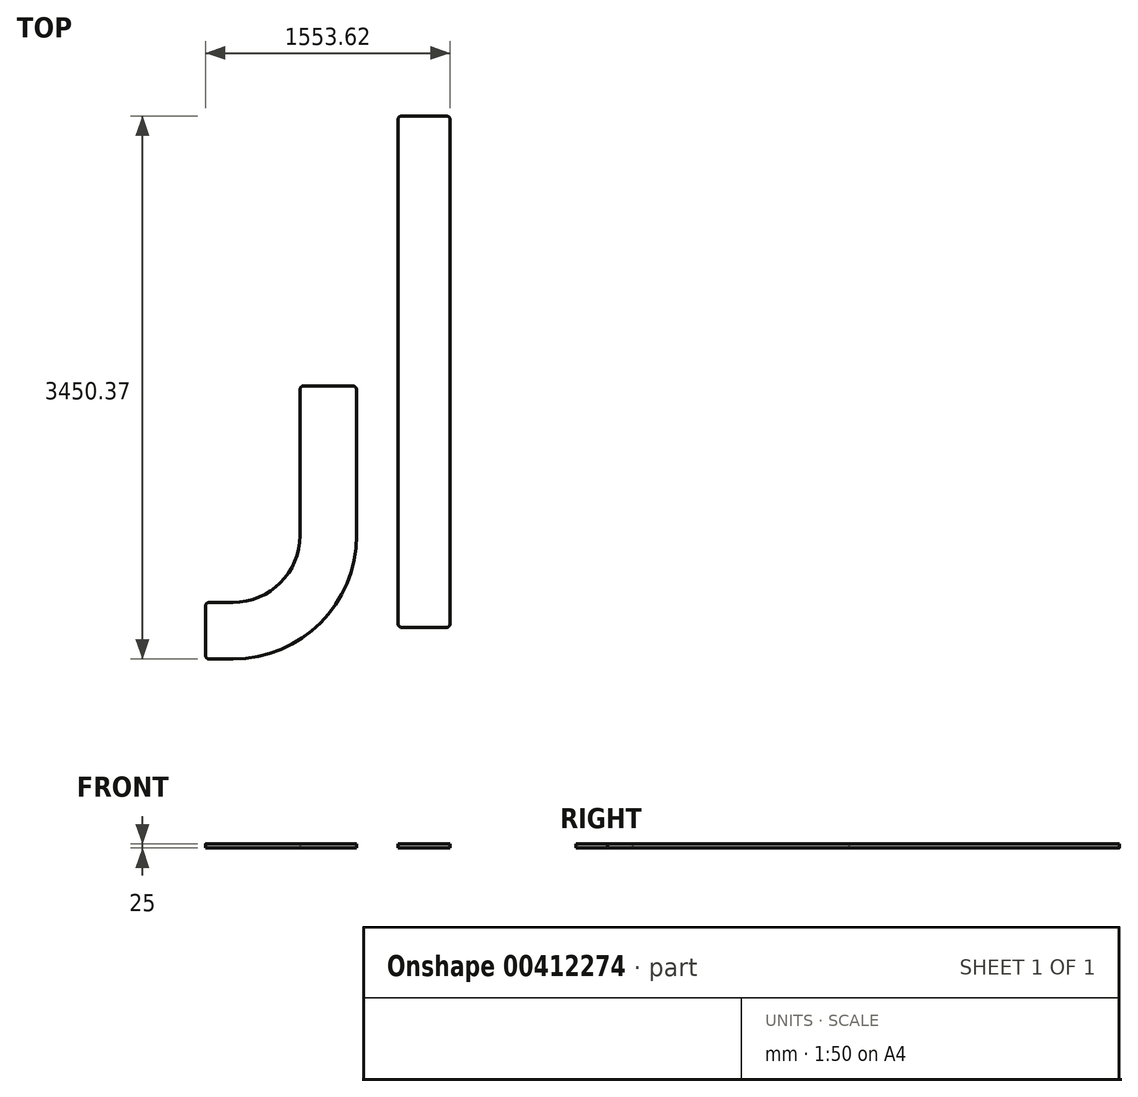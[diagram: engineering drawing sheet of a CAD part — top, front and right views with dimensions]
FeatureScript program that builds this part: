
annotation { "Feature Type Name" : "Feature", "Feature Type Description" : "" }
export const myFeature = defineFeature(function(context is Context, id is Id, definition is map)
    precondition{}
    {
        {
            var Q0;
            Q0=qCreatedBy(makeId("Top.planeOp"),FACE);
            var sketch = newSketch(context, id + "F0", { "sketchPlane" : qUnion([Q0])});
            skLineSegment(sketch, "E0.top", {"start": v(0, 950) * mm, "end": v(360, 950) * mm});
            skLineSegment(sketch, "E0.left", {"start": v(0, 0) * mm, "end": v(0, 950) * mm});
            skLineSegment(sketch, "E0.right", {"start": v(360, 0) * mm, "end": v(360, 950) * mm});
            skArc(sketch, "E1", {"start": v(-425, -425) * mm, "mid": v(-124.48, -300.52) * mm, "end": v(0, 0) * mm});
            skArc(sketch, "E2", {"start": v(-425, -785) * mm, "mid": v(130.08, -555.08) * mm, "end": v(360, 0) * mm});
            skLineSegment(sketch, "E3", {"start": v(-425, -425) * mm, "end": v(-600, -425) * mm});
            skLineSegment(sketch, "E4", {"start": v(-425, -785) * mm, "end": v(-600, -785) * mm});
            skLineSegment(sketch, "E5", {"start": v(-600, -785) * mm, "end": v(-600, -425) * mm});
            skSolve(sketch);
        }
        {
            var Q0;
            Q0=makeQuery(id+"F0.imprint","IMPRINT",FACE,{"disambiguationData":[TD([[makeQuery(id+"F0.imprint","IMPRINT",EDGE,{"derivedFrom":sQuery(id+"F0.wireOp",EDGE,"E0.top")}),-1.0]])]});
            extrude(context, id + "F1", {"entities" : qUnion([Q0]), "depth" : 25 * mm});
        }
        {
            var Q0;
            Q0=makeQuery(id+"F1.opExtrude","SWEPT_EDGE",EDGE,{"disambiguationData":[OSD([sQuery(id+"F0.wireOp",EDGE,"E0.top"),sQuery(id+"F0.wireOp",EDGE,"E0.left")])]});
            var Q1;
            Q1=makeQuery(id+"F1.opExtrude","SWEPT_EDGE",EDGE,{"disambiguationData":[OSD([sQuery(id+"F0.wireOp",EDGE,"E0.top"),sQuery(id+"F0.wireOp",EDGE,"E0.right")])]});
            var Q2;
            Q2=makeQuery(id+"F1.opExtrude","SWEPT_EDGE",EDGE,{"disambiguationData":[OSD([sQuery(id+"F0.wireOp",EDGE,"E4"),sQuery(id+"F0.wireOp",EDGE,"E5")])]});
            var Q3;
            Q3=makeQuery(id+"F1.opExtrude","SWEPT_EDGE",EDGE,{"disambiguationData":[OSD([sQuery(id+"F0.wireOp",EDGE,"E3"),sQuery(id+"F0.wireOp",EDGE,"E5")])]});
            fillet(context, id + "F2", {"entities" : qUnion([Q0, Q1, Q2, Q3]), "radius" : 25 * mm, "tangentPropagation" : true, "allowEdgeOverflow" : false});
        }
        {
            var Q0;
            Q0=qCreatedBy(makeId("Top.planeOp"),FACE);
            var sketch = newSketch(context, id + "F3", { "sketchPlane" : qUnion([Q0])});
            skLineSegment(sketch, "E6.bottom", {"start": v(623.62, 2665.37) * mm, "end": v(953.62, 2665.37) * mm});
            skLineSegment(sketch, "E6.top", {"start": v(623.62, -584.63) * mm, "end": v(953.62, -584.63) * mm});
            skLineSegment(sketch, "E6.left", {"start": v(623.62, 2665.37) * mm, "end": v(623.62, -584.63) * mm});
            skLineSegment(sketch, "E6.right", {"start": v(953.62, 2665.37) * mm, "end": v(953.62, -584.63) * mm});
            skSolve(sketch);
        }
        {
            var Q0;
            Q0=makeQuery(id+"F3.imprint","IMPRINT",FACE,{"disambiguationData":[TD([[makeQuery(id+"F3.imprint","IMPRINT",EDGE,{"derivedFrom":sQuery(id+"F3.wireOp",EDGE,"E6.bottom")}),-1.0]])]});
            extrude(context, id + "F4", {"entities" : qUnion([Q0]), "depth" : 25 * mm});
        }
        {
            var Q0;
            Q0=makeQuery(id+"F4.opExtrude","SWEPT_EDGE",EDGE,{"disambiguationData":[OSD([sQuery(id+"F3.wireOp",EDGE,"E6.bottom"),sQuery(id+"F3.wireOp",EDGE,"E6.left")])]});
            var Q1;
            Q1=makeQuery(id+"F4.opExtrude","SWEPT_EDGE",EDGE,{"disambiguationData":[OSD([sQuery(id+"F3.wireOp",EDGE,"E6.bottom"),sQuery(id+"F3.wireOp",EDGE,"E6.right")])]});
            var Q2;
            Q2=makeQuery(id+"F4.opExtrude","SWEPT_EDGE",EDGE,{"disambiguationData":[OSD([sQuery(id+"F3.wireOp",EDGE,"E6.top"),sQuery(id+"F3.wireOp",EDGE,"E6.right")])]});
            var Q3;
            Q3=makeQuery(id+"F4.opExtrude","SWEPT_EDGE",EDGE,{"disambiguationData":[OSD([sQuery(id+"F3.wireOp",EDGE,"E6.top"),sQuery(id+"F3.wireOp",EDGE,"E6.left")])]});
            fillet(context, id + "F5", {"entities" : qUnion([Q0, Q1, Q2, Q3]), "radius" : 25 * mm, "tangentPropagation" : true, "allowEdgeOverflow" : false});
        }
    });
